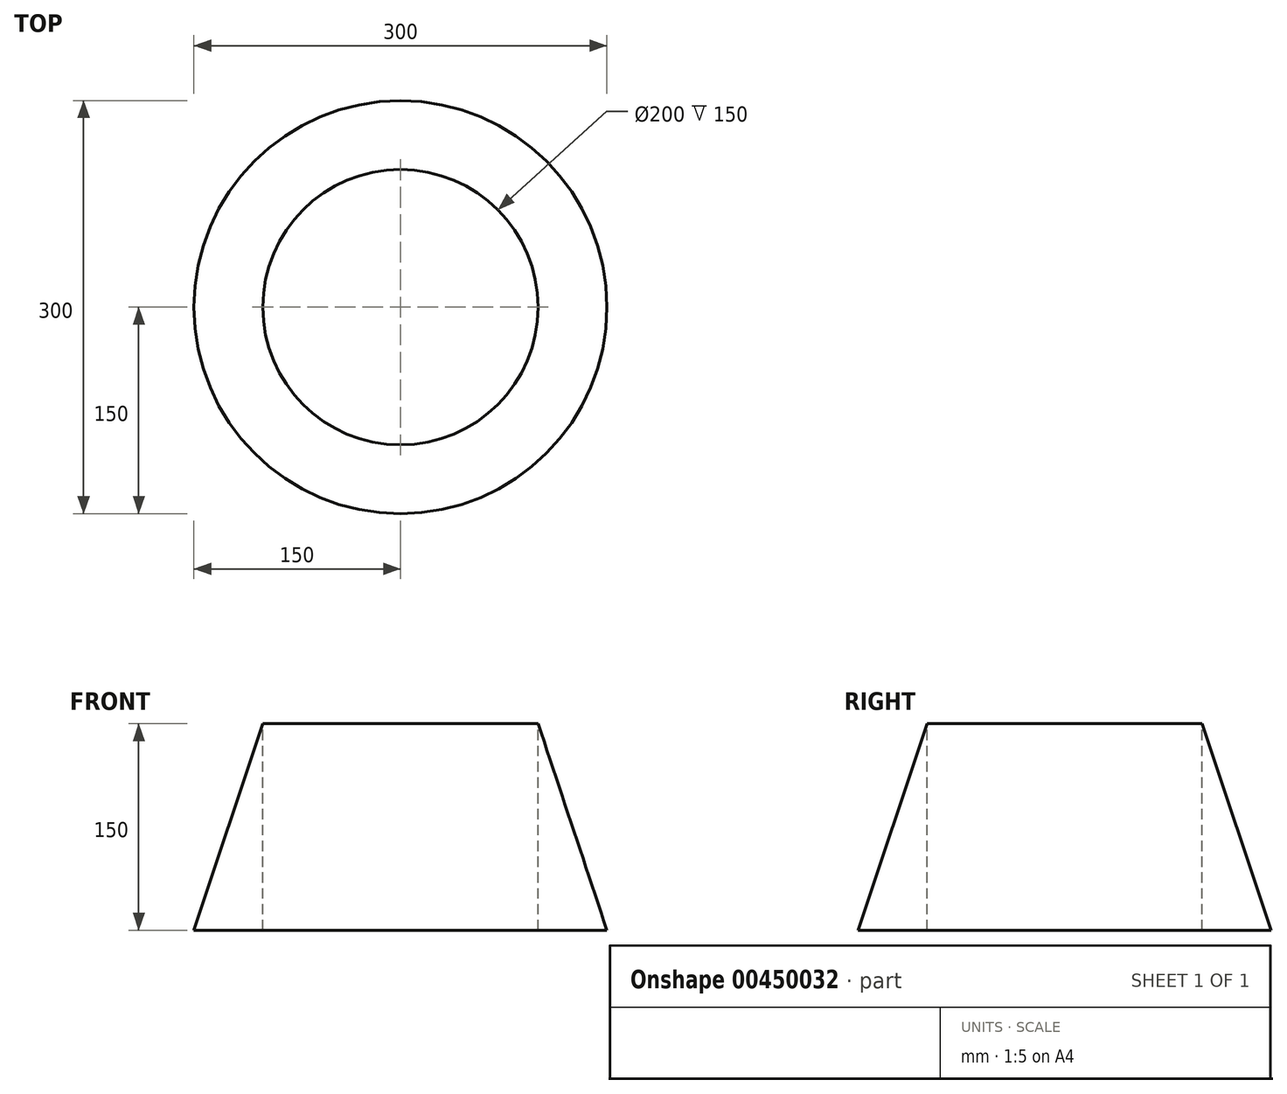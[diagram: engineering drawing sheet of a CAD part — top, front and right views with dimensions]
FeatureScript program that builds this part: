
annotation { "Feature Type Name" : "Feature", "Feature Type Description" : "" }
export const myFeature = defineFeature(function(context is Context, id is Id, definition is map)
    precondition{}
    {
        {
            var Q0;
            Q0=qCreatedBy(makeId("Front.planeOp"),FACE);
            var sketch = newSketch(context, id + "F0", { "sketchPlane" : qUnion([Q0])});
            skLineSegment(sketch, "E0", {"start": v(0, 150) * mm, "end": v(100, 150) * mm});
            skLineSegment(sketch, "E1", {"start": v(0, 150) * mm, "end": v(0, 0) * mm});
            skLineSegment(sketch, "E2", {"start": v(100, 150) * mm, "end": v(150, 0) * mm});
            skLineSegment(sketch, "E3", {"start": v(0, 0) * mm, "end": v(150, 0) * mm});
            skSolve(sketch);
        }
        {
            var Q0;
            Q0 = qSketchRegion(id + "F0", true);
            var Q1;
            Q1=sQuery(id+"F0.wireOp",EDGE,"E1");
            revolve(context, id + "F1", {"entities" : qUnion([Q0]), "axis" : qUnion([Q1]), "revolveType" : RevolveType.FULL});
        }
        {
            var Q0;
            Q0=makeQuery(id+"F1.opRevolve","SWEPT_FACE",FACE,{"disambiguationData":[OSD([sQuery(id+"F0.wireOp",EDGE,"E0")])]});
            extrude(context, id + "F2", {"entities" : qUnion([Q0]), "operationType" : NewBodyOperationType.REMOVE, "oppositeDirection" : true, "depth" : 225 * mm});
        }
    });
